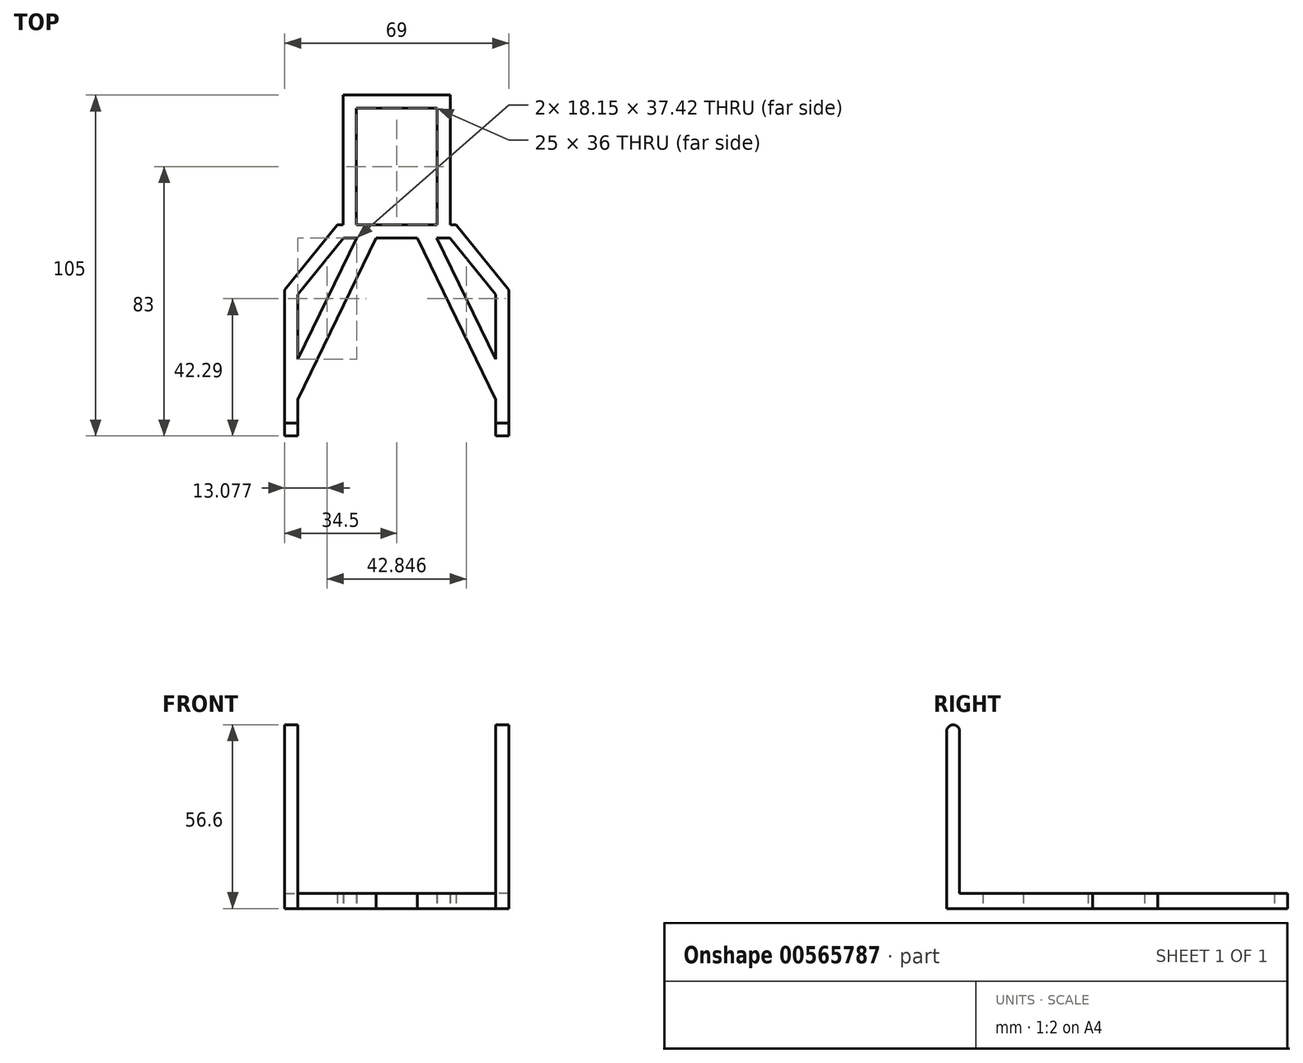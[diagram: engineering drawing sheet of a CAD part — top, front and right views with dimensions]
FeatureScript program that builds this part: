
annotation { "Feature Type Name" : "Feature", "Feature Type Description" : "" }
export const myFeature = defineFeature(function(context is Context, id is Id, definition is map)
    precondition{}
    {
        {
            var Q0;
            Q0=qCreatedBy(makeId("Top.planeOp"),FACE);
            var sketch = newSketch(context, id + "F0", { "sketchPlane" : qUnion([Q0])});
            skLineSegment(sketch, "E0", {"start": v(-16.5, 0) * mm, "end": v(16.5, 0) * mm});
            skLineSegment(sketch, "E1", {"start": v(16.5, 0) * mm, "end": v(16.5, -40) * mm});
            skLineSegment(sketch, "E2", {"start": v(-16.5, 0) * mm, "end": v(-16.5, -40) * mm});
            skLineSegment(sketch, "E3", {"start": v(-18.25, -40) * mm, "end": v(18.25, -40) * mm});
            skLineSegment(sketch, "E4.bottom", {"start": v(-12.5, -40) * mm, "end": v(12.5, -40) * mm});
            skLineSegment(sketch, "E4.top", {"start": v(-12.5, -4) * mm, "end": v(12.5, -4) * mm});
            skLineSegment(sketch, "E4.left", {"start": v(-12.5, -40) * mm, "end": v(-12.5, -4) * mm});
            skLineSegment(sketch, "E4.right", {"start": v(12.5, -40) * mm, "end": v(12.5, -4) * mm});
            skLineSegment(sketch, "E5", {"start": v(-18.25, -40) * mm, "end": v(-34.5, -60) * mm});
            skLineSegment(sketch, "E6", {"start": v(-34.5, -60) * mm, "end": v(-34.5, -105) * mm});
            skLineSegment(sketch, "E7", {"start": v(18.25, -40) * mm, "end": v(34.5, -60) * mm});
            skLineSegment(sketch, "E8", {"start": v(34.5, -60) * mm, "end": v(34.5, -105) * mm});
            skLineSegment(sketch, "E9", {"start": v(-34.5, -105) * mm, "end": v(-30.5, -105) * mm});
            skLineSegment(sketch, "E10", {"start": v(-30.5, -105) * mm, "end": v(-30.5, -61.42) * mm});
            skLineSegment(sketch, "E11", {"start": v(-30.5, -61.42) * mm, "end": v(-16.35, -44) * mm});
            skLineSegment(sketch, "E12", {"start": v(-16.35, -44) * mm, "end": v(16.35, -44) * mm});
            skLineSegment(sketch, "E13", {"start": v(16.35, -44) * mm, "end": v(30.5, -61.42) * mm});
            skLineSegment(sketch, "E14", {"start": v(30.5, -61.42) * mm, "end": v(30.5, -105) * mm});
            skLineSegment(sketch, "E15", {"start": v(30.5, -105) * mm, "end": v(34.5, -105) * mm});
            skLineSegment(sketch, "E16", {"start": v(-6.34, -44) * mm, "end": v(-30.5, -93.8) * mm});
            skLineSegment(sketch, "E17", {"start": v(-12.35, -44) * mm, "end": v(-30.5, -81.42) * mm});
            skLineSegment(sketch, "E18.MirrorCS", {"start": v(12.35, -44) * mm, "end": v(30.5, -81.42) * mm});
            skLineSegment(sketch, "E19.MirrorCS", {"start": v(6.34, -44) * mm, "end": v(30.5, -93.8) * mm});
            skSolve(sketch);
        }
        {
            var Q0;
            Q0 = qSketchRegion(id + "F0", true);
            extrude(context, id + "F1", {"entities" : qUnion([Q0]), "depth" : 4.6 * mm, "offsetDistance" : 25 * mm});
        }
        {
            var Q0;
            Q0=makeQuery(id+"F1.opExtrude","CAP_FACE",FACE,{"disambiguationData":[OSD([sQuery(id+"F0.wireOp",EDGE,"E0"),sQuery(id+"F0.wireOp",EDGE,"E1"),sQuery(id+"F0.wireOp",EDGE,"E2"),sQuery(id+"F0.wireOp",EDGE,"E3"),sQuery(id+"F0.wireOp",EDGE,"E4.bottom"),sQuery(id+"F0.wireOp",EDGE,"E4.top"),sQuery(id+"F0.wireOp",EDGE,"E4.left"),sQuery(id+"F0.wireOp",EDGE,"E4.right"),sQuery(id+"F0.wireOp",EDGE,"E5"),sQuery(id+"F0.wireOp",EDGE,"E6"),sQuery(id+"F0.wireOp",EDGE,"E7"),sQuery(id+"F0.wireOp",EDGE,"E8"),sQuery(id+"F0.wireOp",EDGE,"E9"),sQuery(id+"F0.wireOp",EDGE,"E10"),sQuery(id+"F0.wireOp",EDGE,"E11"),sQuery(id+"F0.wireOp",EDGE,"E12"),sQuery(id+"F0.wireOp",EDGE,"E13"),sQuery(id+"F0.wireOp",EDGE,"E14"),sQuery(id+"F0.wireOp",EDGE,"E15"),sQuery(id+"F0.wireOp",EDGE,"E16"),sQuery(id+"F0.wireOp",EDGE,"E17"),sQuery(id+"F0.wireOp",EDGE,"E18.MirrorCS"),sQuery(id+"F0.wireOp",EDGE,"E19.MirrorCS")])],"isStart":false});
            var sketch = newSketch(context, id + "F2", { "sketchPlane" : qUnion([Q0])});
            skLineSegment(sketch, "E20.bottom", {"start": v(-34.5, -105) * mm, "end": v(-30.5, -105) * mm});
            skLineSegment(sketch, "E20.top", {"start": v(-34.5, -101) * mm, "end": v(-30.5, -101) * mm});
            skLineSegment(sketch, "E20.left", {"start": v(-34.5, -105) * mm, "end": v(-34.5, -101) * mm});
            skLineSegment(sketch, "E20.right", {"start": v(-30.5, -105) * mm, "end": v(-30.5, -101) * mm});
            skLineSegment(sketch, "E21.MirrorCS", {"start": v(30.5, -105) * mm, "end": v(30.5, -101) * mm});
            skLineSegment(sketch, "E22.MirrorCS", {"start": v(34.5, -105) * mm, "end": v(34.5, -101) * mm});
            skLineSegment(sketch, "E23.MirrorCS", {"start": v(34.5, -101) * mm, "end": v(30.5, -101) * mm});
            skLineSegment(sketch, "E24.MirrorCS", {"start": v(34.5, -105) * mm, "end": v(30.5, -105) * mm});
            skSolve(sketch);
        }
        {
            var Q0;
            Q0 = qSketchRegion(id + "F2", true);
            extrude(context, id + "F3", {"entities" : qUnion([Q0]), "operationType" : NewBodyOperationType.ADD, "depth" : 52 * mm, "offsetDistance" : 25 * mm});
        }
        {
            var Q0;
            Q0=makeQuery(id+"F3.opExtrude","CAP_EDGE",EDGE,{"disambiguationData":[OSD([sQuery(id+"F2.wireOp",EDGE,"E20.bottom")])],"isStart":false});
            var Q1;
            Q1=makeQuery(id+"F3.opExtrude","CAP_EDGE",EDGE,{"disambiguationData":[OSD([sQuery(id+"F2.wireOp",EDGE,"E20.top")])],"isStart":false});
            var Q2;
            Q2=makeQuery(id+"F3.opExtrude","CAP_EDGE",EDGE,{"disambiguationData":[OSD([sQuery(id+"F2.wireOp",EDGE,"E24.MirrorCS")])],"isStart":false});
            var Q3;
            Q3=makeQuery(id+"F3.opExtrude","CAP_EDGE",EDGE,{"disambiguationData":[OSD([sQuery(id+"F2.wireOp",EDGE,"E23.MirrorCS")])],"isStart":false});
            fillet(context, id + "F4", {"entities" : qUnion([Q0, Q1, Q2, Q3]), "radius" : 2 * mm, "tangentPropagation" : true, "allowEdgeOverflow" : false});
        }
    });
